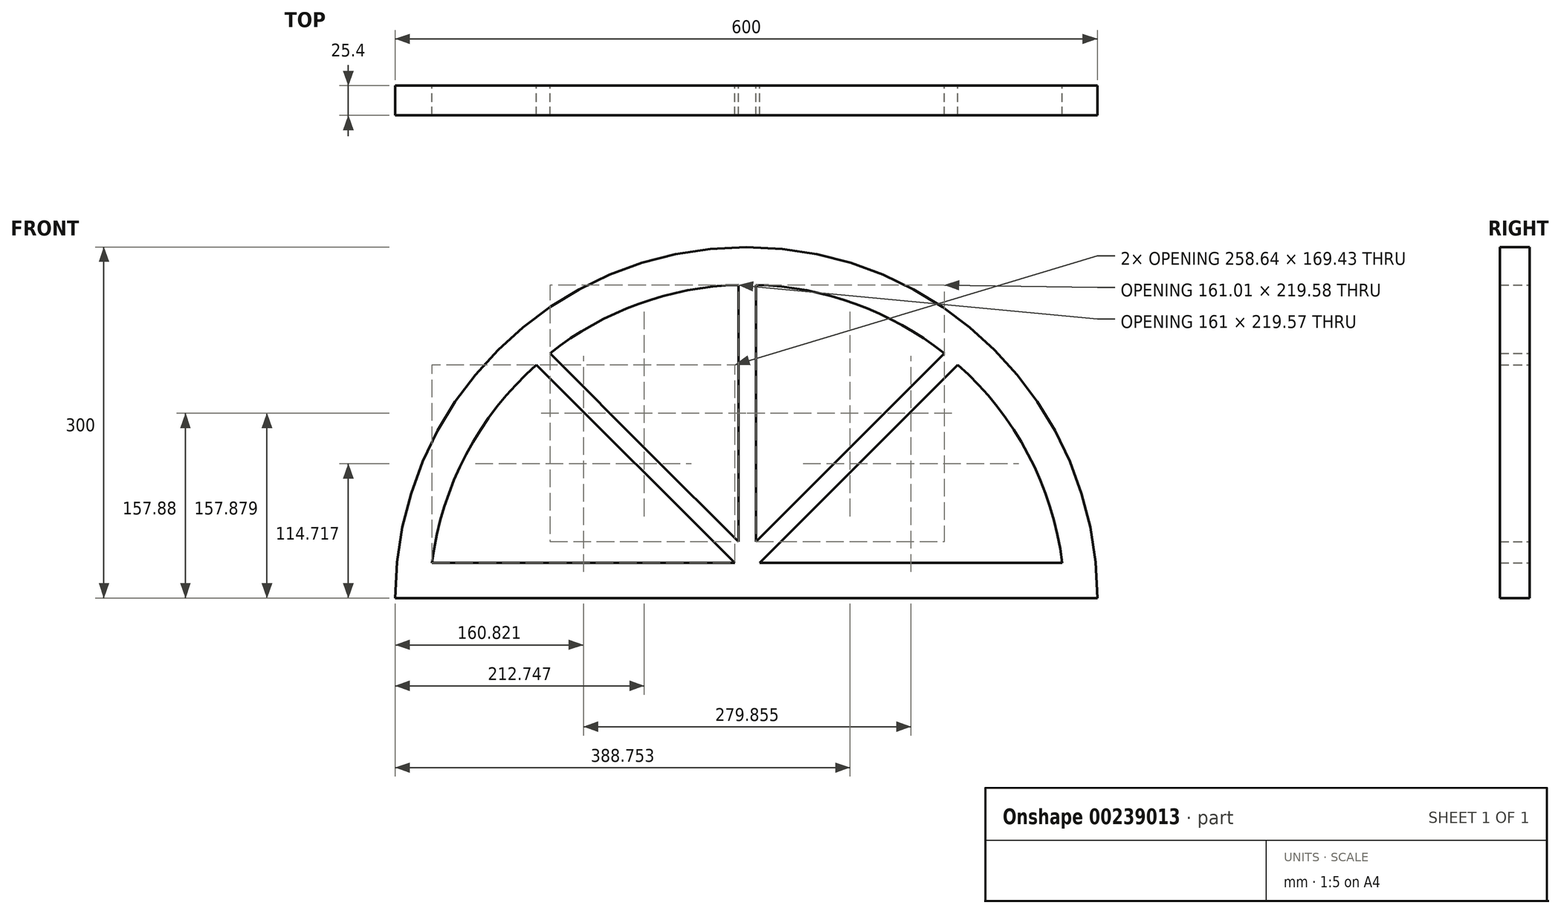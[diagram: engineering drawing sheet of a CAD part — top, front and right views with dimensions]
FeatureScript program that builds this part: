
annotation { "Feature Type Name" : "Feature", "Feature Type Description" : "" }
export const myFeature = defineFeature(function(context is Context, id is Id, definition is map)
    precondition{}
    {
        {
            var Q0;
            Q0=qCreatedBy(makeId("Front.planeOp"),FACE);
            var sketch = newSketch(context, id + "F0", { "sketchPlane" : qUnion([Q0])});
            skLineSegment(sketch, "E0", {"start": v(-31.5, 13.21) * mm, "end": v(568.5, 13.21) * mm});
            skArc(sketch, "E1", {"start": v(568.5, 13.21) * mm, "mid": v(268.5, 313.21) * mm, "end": v(-31.5, 13.21) * mm});
            skLineSegment(sketch, "E2", {"start": v(-31.5, 13.21) * mm, "end": v(0, 13.21) * mm});
            skArc(sketch, "E3", {"start": v(538.5, 43.21) * mm, "mid": v(451.65, 210.53) * mm, "end": v(276.75, 280.88) * mm});
            skLineSegment(sketch, "E4", {"start": v(0, 43.21) * mm, "end": v(258.64, 43.21) * mm});
            skLineSegment(sketch, "E5", {"start": v(371.55, 145.51) * mm, "end": v(371.76, 145.72) * mm});
            skLineSegment(sketch, "E6", {"start": v(366.66, 151.22) * mm, "end": v(269.25, 53.8) * mm});
            skLineSegment(sketch, "E7", {"start": v(366.66, 151.22) * mm, "end": v(437.76, 222.31) * mm});
            skLineSegment(sketch, "E8", {"start": v(376.85, 140.21) * mm, "end": v(449.29, 212.64) * mm});
            skLineSegment(sketch, "E9", {"start": v(376.85, 140.21) * mm, "end": v(279.85, 43.21) * mm});
            skLineSegment(sketch, "E10", {"start": v(176.77, 125.08) * mm, "end": v(258.64, 43.21) * mm});
            skLineSegment(sketch, "E11", {"start": v(176.77, 125.08) * mm, "end": v(89.2, 212.64) * mm});
            skLineSegment(sketch, "E12", {"start": v(187.38, 135.69) * mm, "end": v(100.75, 222.32) * mm});
            skLineSegment(sketch, "E13", {"start": v(187.38, 135.69) * mm, "end": v(269.25, 53.8) * mm});
            skLineSegment(sketch, "E14", {"start": v(261.75, 162.1) * mm, "end": v(261.75, 61.3) * mm});
            skLineSegment(sketch, "E15", {"start": v(276.75, 162.1) * mm, "end": v(276.75, 61.3) * mm});
            skLineSegment(sketch, "E16", {"start": v(276.75, 162.1) * mm, "end": v(276.75, 280.88) * mm});
            skLineSegment(sketch, "E17", {"start": v(261.75, 162.1) * mm, "end": v(261.75, 280.88) * mm});
            skPoint(sketch, "E18.orphan", {"position": v(94.9, 217.56) * mm});
            skPoint(sketch, "E19.start.orphan", {"position": v(182.08, 130.38) * mm});
            skArc(sketch, "E20.trimOffspring", {"start": v(89.2, 212.64) * mm, "mid": v(29.16, 136.06) * mm, "end": v(0, 43.21) * mm});
            skPoint(sketch, "E21.start.orphan", {"position": v(269.25, 162.1) * mm});
            skPoint(sketch, "E22.trimOffspring.end.orphan", {"position": v(269.25, 280.98) * mm});
            skArc(sketch, "E23.trimOffspring", {"start": v(261.75, 280.88) * mm, "mid": v(176.5, 264.64) * mm, "end": v(100.75, 222.32) * mm});
            skLineSegment(sketch, "E24.trimOffspring", {"start": v(279.85, 43.21) * mm, "end": v(538.5, 43.21) * mm});
            skPoint(sketch, "E25.orphan", {"position": v(269.25, 43.21) * mm});
            skSolve(sketch);
        }
        {
            var Q0;
            Q0=makeQuery(id+"F0.imprint","IMPRINT",FACE,{"disambiguationData":[TD([[makeQuery(id+"F0.imprint","IMPRINT",EDGE,{"derivedFrom":sQuery(id+"F0.wireOp",EDGE,"E0")}),1.0]])]});
            extrude(context, id + "F1", {"entities" : qUnion([Q0]), "depth" : 25.4 * mm});
        }
    });
